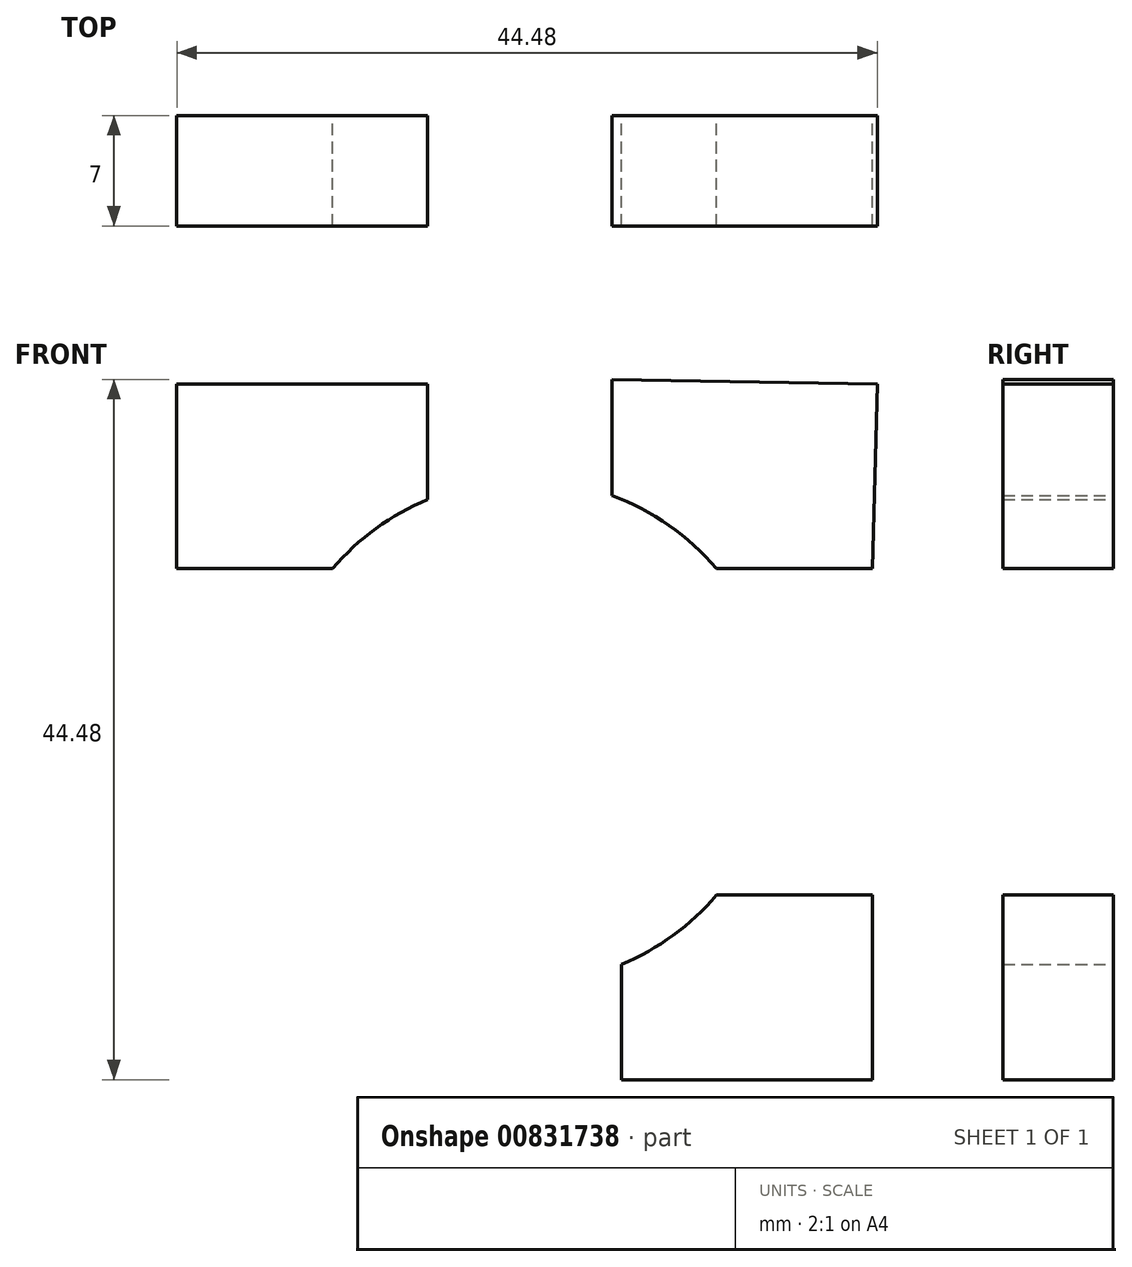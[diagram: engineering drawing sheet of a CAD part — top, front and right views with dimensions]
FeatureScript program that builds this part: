
annotation { "Feature Type Name" : "Feature", "Feature Type Description" : "" }
export const myFeature = defineFeature(function(context is Context, id is Id, definition is map)
    precondition{}
    {
        {
            var Q0;
            Q0=qCreatedBy(makeId("Front.planeOp"),FACE);
            var sketch = newSketch(context, id + "F0", { "sketchPlane" : qUnion([Q0])});
            skCircle(sketch, "E0", {"center": v(0, 0) * mm, "radius": 16 * mm});
            skLineSegment(sketch, "E1.top", {"start": v(-22.1, -22.4) * mm, "end": v(22.4, -22.4) * mm});
            skLineSegment(sketch, "E2.bottom", {"start": v(-22.1, 10.37) * mm, "end": v(-6.16, 10.37) * mm});
            skLineSegment(sketch, "E2.top", {"start": v(-22.1, 22.1) * mm, "end": v(-6.16, 22.1) * mm});
            skLineSegment(sketch, "E2.left", {"start": v(-22.1, 10.37) * mm, "end": v(-22.1, 22.1) * mm});
            skLineSegment(sketch, "E2.right", {"start": v(-6.16, 10.37) * mm, "end": v(-6.16, 22.1) * mm});
            skLineSegment(sketch, "E3.1.0", {"start": v(22.1, -10.37) * mm, "end": v(22.1, -22.1) * mm});
            skLineSegment(sketch, "E3.1.1", {"start": v(22.1, -10.37) * mm, "end": v(6.16, -10.37) * mm});
            skLineSegment(sketch, "E3.1.2", {"start": v(6.16, -10.37) * mm, "end": v(6.16, -22.1) * mm});
            skLineSegment(sketch, "E3.1.3", {"start": v(22.1, -22.1) * mm, "end": v(6.16, -22.1) * mm});
            skLineSegment(sketch, "E4.bottom", {"start": v(-22.1, -10.37) * mm, "end": v(-5.56, -10.37) * mm});
            skLineSegment(sketch, "E4.top", {"start": v(-22.1, -22.4) * mm, "end": v(-5.56, -22.4) * mm});
            skLineSegment(sketch, "E4.left", {"start": v(-22.1, -10.37) * mm, "end": v(-22.1, -22.4) * mm});
            skLineSegment(sketch, "E4.right", {"start": v(-5.56, -10.37) * mm, "end": v(-5.56, -22.4) * mm});
            skLineSegment(sketch, "E5.1.0", {"start": v(22.1, 10.37) * mm, "end": v(5.56, 10.37) * mm});
            skLineSegment(sketch, "E5.1.1", {"start": v(5.56, 10.37) * mm, "end": v(5.56, 22.4) * mm});
            skLineSegment(sketch, "E5.1.2", {"start": v(22.1, 22.4) * mm, "end": v(5.56, 22.4) * mm});
            skLineSegment(sketch, "E6", {"start": v(22.4, 22.1) * mm, "end": v(22.1, 10.37) * mm});
            skLineSegment(sketch, "E7", {"start": v(22.4, 22.1) * mm, "end": v(5.56, 22.4) * mm});
            skSolve(sketch);
        }
        {
            var Q0;
            {var subQ1=sQuery(id+"F0.wireOp",EDGE,"E2.top");Q0=makeQuery(id+"F0.imprint","IMPRINT",FACE,{"disambiguationData":[TD([[makeQuery(id+"F0.imprint","IMPRINT",EDGE,{"derivedFrom":subQ1}),-1.0]])]});}
            var Q1;
            {var subQ4=sQuery(id+"F0.wireOp",EDGE,"E6");Q1=makeQuery(id+"F0.imprint","IMPRINT",FACE,{"disambiguationData":[TD([[makeQuery(id+"F0.imprint","IMPRINT",EDGE,{"derivedFrom":subQ4}),-1.0]])]});}
            var Q2;
            {var subQ1=sQuery(id+"F0.wireOp",EDGE,"E4.top");Q2=makeQuery(id+"F0.imprint","IMPRINT",FACE,{"disambiguationData":[TD([[makeQuery(id+"F0.imprint","IMPRINT",EDGE,{"derivedFrom":subQ1}),1.0]])]});}
            var Q3;
            {var subQ5=sQuery(id+"F0.wireOp",EDGE,"E3.1.0");Q3=makeQuery(id+"F0.imprint","IMPRINT",FACE,{"disambiguationData":[TD([[makeQuery(id+"F0.imprint","IMPRINT",EDGE,{"derivedFrom":subQ5}),-1.0]])]});}
            extrude(context, id + "F1", {"entities" : qUnion([Q0, Q1, Q2, Q3]), "depth" : 7 * mm, "offsetDistance" : 25 * mm});
        }
        {
            var Q0;
            Q0=qCreatedBy(makeId("Front.planeOp"),FACE);
            var sketch = newSketch(context, id + "F2", { "sketchPlane" : qUnion([Q0])});
            skLineSegment(sketch, "E8.bottom", {"start": v(-21.5, 10.37) * mm, "end": v(21.5, 10.37) * mm});
            skLineSegment(sketch, "E8.top", {"start": v(-21.5, -10.37) * mm, "end": v(21.5, -10.37) * mm});
            skLineSegment(sketch, "E8.left", {"start": v(-21.5, 10.37) * mm, "end": v(-21.5, -10.37) * mm});
            skLineSegment(sketch, "E8.right", {"start": v(21.5, 10.37) * mm, "end": v(21.5, -10.37) * mm});
            skPoint(sketch, "E8.middle", {"position": v(0, 0) * mm});
            skSolve(sketch);
        }
        {
            var Q0;
            Q0=qCreatedBy(makeId("Front.planeOp"),FACE);
            var sketch = newSketch(context, id + "F3", { "sketchPlane" : qUnion([Q0])});
            skLineSegment(sketch, "E9.bottom", {"start": v(-6.16, 22.4) * mm, "end": v(6.16, 22.4) * mm});
            skLineSegment(sketch, "E9.top", {"start": v(-6.16, 0.15) * mm, "end": v(6.16, 0.15) * mm});
            skLineSegment(sketch, "E9.left", {"start": v(-6.16, 22.4) * mm, "end": v(-6.16, 0.15) * mm});
            skLineSegment(sketch, "E9.right", {"start": v(6.16, 22.4) * mm, "end": v(6.16, 0.15) * mm});
            skPoint(sketch, "E9.middle", {"position": v(0, 11.27) * mm});
            skSolve(sketch);
        }
        {
            var Q0;
            Q0=qCreatedBy(makeId("Front.planeOp"),FACE);
            var sketch = newSketch(context, id + "F4", { "sketchPlane" : qUnion([Q0])});
            skLineSegment(sketch, "E10.bottom", {"start": v(5.56, -22.1) * mm, "end": v(-5.56, -22.1) * mm});
            skLineSegment(sketch, "E10.top", {"start": v(5.56, -0.45) * mm, "end": v(-5.56, -0.45) * mm});
            skLineSegment(sketch, "E10.left", {"start": v(5.56, -22.1) * mm, "end": v(5.56, -0.45) * mm});
            skLineSegment(sketch, "E10.right", {"start": v(-5.56, -22.1) * mm, "end": v(-5.56, -0.45) * mm});
            skPoint(sketch, "E10.middle", {"position": v(0, -11.27) * mm});
            skSolve(sketch);
        }
        {
            var Q0;
            Q0=qCreatedBy(makeId("Front.planeOp"),FACE);
            var sketch = newSketch(context, id + "F5", { "sketchPlane" : qUnion([Q0])});
            skCircle(sketch, "E11", {"center": v(0, 0) * mm, "radius": 15.66 * mm});
            skSolve(sketch);
        }
        {
            var Q0;
            Q0=makeQuery(id+"F2.imprint","IMPRINT",FACE,{"disambiguationData":[TD([[makeQuery(id+"F2.imprint","IMPRINT",EDGE,{"derivedFrom":sQuery(id+"F2.wireOp",EDGE,"E8.bottom")}),-1.0]])]});
            var Q1;
            Q1=makeQuery(id+"F3.imprint","IMPRINT",FACE,{"disambiguationData":[TD([[makeQuery(id+"F3.imprint","IMPRINT",EDGE,{"derivedFrom":sQuery(id+"F3.wireOp",EDGE,"E9.bottom")}),-1.0]])]});
            var Q2;
            Q2=makeQuery(id+"F5.imprint","IMPRINT",FACE,{"disambiguationData":[TD([[makeQuery(id+"F5.imprint","IMPRINT",EDGE,{"derivedFrom":sQuery(id+"F5.wireOp",EDGE,"E11")}),1.0]])]});
            var Q3;
            Q3=makeQuery(id+"F4.imprint","IMPRINT",FACE,{"disambiguationData":[TD([[makeQuery(id+"F4.imprint","IMPRINT",EDGE,{"derivedFrom":sQuery(id+"F4.wireOp",EDGE,"E10.bottom")}),-1.0]])]});
            extrude(context, id + "F6", {"entities" : qUnion([Q0, Q1, Q2, Q3]), "depth" : 25 * mm, "offsetDistance" : 25 * mm});
        }
        {
            var Q0;
            Q0=makeQuery(id+"F6.opExtrude","SWEPT_BODY",BODY,{"disambiguationData":[OSD([sQuery(id+"F5.wireOp",EDGE,"E11")])]});
            deleteBodies(context, id + "F7", {"entities" : qUnion([Q0])});
        }
        {
            var Q0;
            Q0=makeQuery(id+"F6.opExtrude","SWEPT_BODY",BODY,{"disambiguationData":[OSD([sQuery(id+"F4.wireOp",EDGE,"E10.bottom"),sQuery(id+"F4.wireOp",EDGE,"E10.top"),sQuery(id+"F4.wireOp",EDGE,"E10.left"),sQuery(id+"F4.wireOp",EDGE,"E10.right")])]});
            deleteBodies(context, id + "F8", {"entities" : qUnion([Q0])});
        }
        {
            var Q0;
            Q0=makeQuery(id+"F6.opExtrude","SWEPT_BODY",BODY,{"disambiguationData":[OSD([sQuery(id+"F3.wireOp",EDGE,"E9.bottom"),sQuery(id+"F3.wireOp",EDGE,"E9.top"),sQuery(id+"F3.wireOp",EDGE,"E9.left"),sQuery(id+"F3.wireOp",EDGE,"E9.right")])]});
            deleteBodies(context, id + "F9", {"entities" : qUnion([Q0])});
        }
        {
            var Q0;
            Q0=makeQuery(id+"F6.opExtrude","SWEPT_BODY",BODY,{"disambiguationData":[OSD([sQuery(id+"F2.wireOp",EDGE,"E8.bottom"),sQuery(id+"F2.wireOp",EDGE,"E8.top"),sQuery(id+"F2.wireOp",EDGE,"E8.left"),sQuery(id+"F2.wireOp",EDGE,"E8.right")])]});
            deleteBodies(context, id + "F10", {"entities" : qUnion([Q0])});
        }
        {
            var Q0;
            Q0=qCreatedBy(makeId("Front.planeOp"),FACE);
            var sketch = newSketch(context, id + "F11", { "sketchPlane" : qUnion([Q0])});
            skLineSegment(sketch, "E12.bottom", {"start": v(-21.8, 10.07) * mm, "end": v(21.8, 10.07) * mm});
            skLineSegment(sketch, "E12.top", {"start": v(-21.8, -10.07) * mm, "end": v(21.8, -10.07) * mm});
            skLineSegment(sketch, "E12.left", {"start": v(-21.8, 10.07) * mm, "end": v(-21.8, -10.07) * mm});
            skLineSegment(sketch, "E12.right", {"start": v(21.8, 10.07) * mm, "end": v(21.8, -10.07) * mm});
            skPoint(sketch, "E12.middle", {"position": v(0, 0) * mm});
            skSolve(sketch);
        }
        {
            var Q0;
            Q0=makeQuery(id+"F11.imprint","IMPRINT",FACE,{"disambiguationData":[TD([[makeQuery(id+"F11.imprint","IMPRINT",EDGE,{"derivedFrom":sQuery(id+"F11.wireOp",EDGE,"E12.bottom")}),-1.0]])]});
            extrude(context, id + "F12", {"entities" : qUnion([Q0]), "depth" : 8.4 * mm, "offsetDistance" : 25 * mm});
        }
        {
            var Q0;
            Q0=makeQuery(id+"F12.opExtrude","SWEPT_BODY",BODY,{"disambiguationData":[OSD([sQuery(id+"F11.wireOp",EDGE,"E12.bottom"),sQuery(id+"F11.wireOp",EDGE,"E12.top"),sQuery(id+"F11.wireOp",EDGE,"E12.left"),sQuery(id+"F11.wireOp",EDGE,"E12.right")])]});
            deleteBodies(context, id + "F13", {"entities" : qUnion([Q0])});
        }
    });
